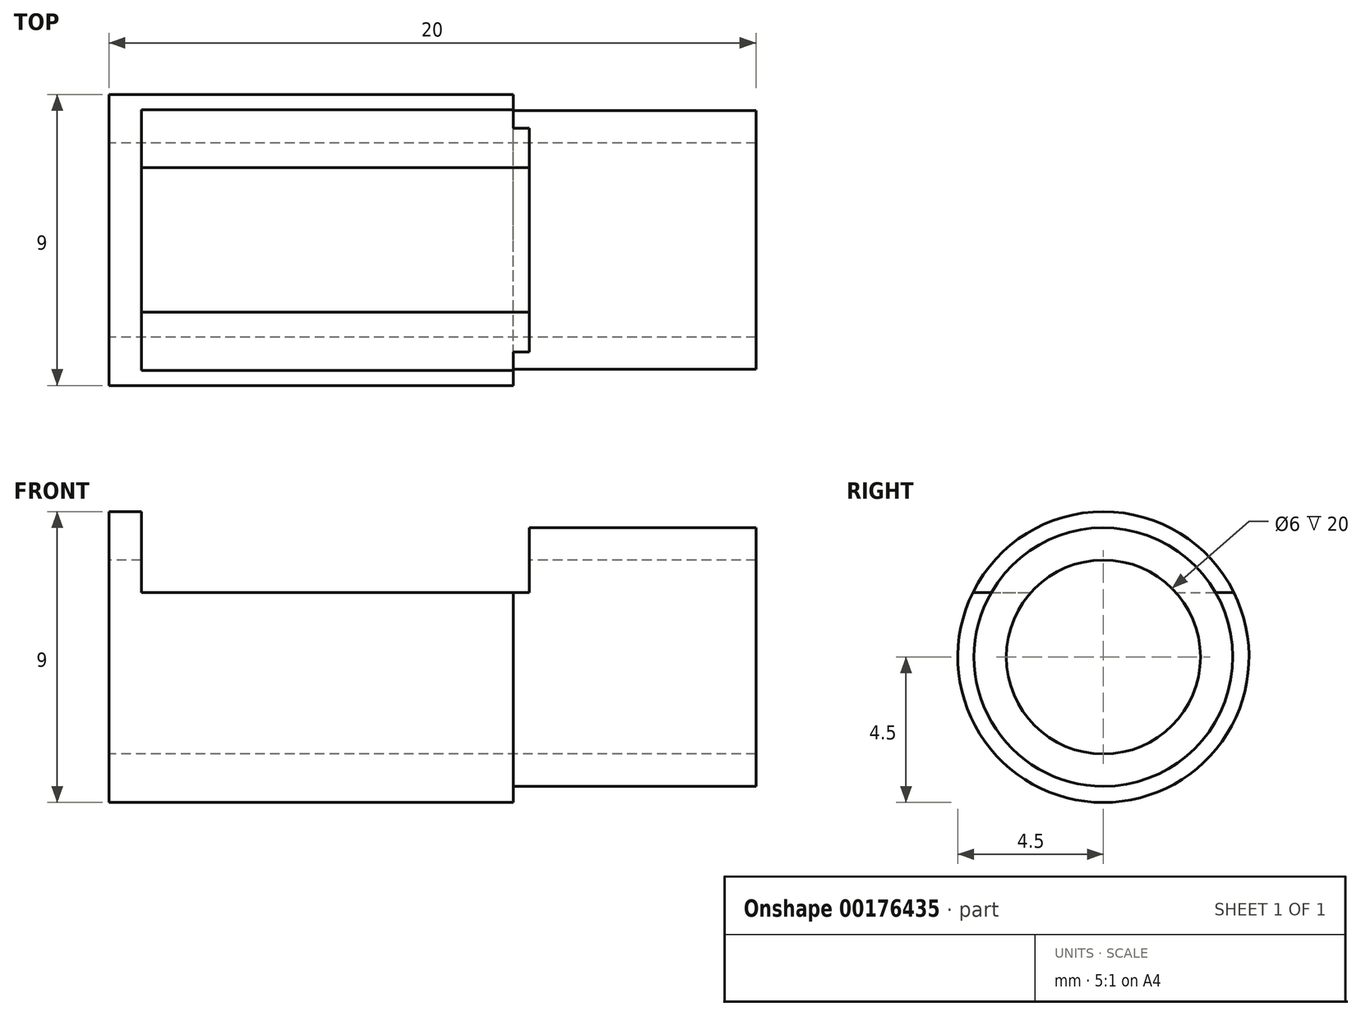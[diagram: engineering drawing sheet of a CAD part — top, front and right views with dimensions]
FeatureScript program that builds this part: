
annotation { "Feature Type Name" : "Feature", "Feature Type Description" : "" }
export const myFeature = defineFeature(function(context is Context, id is Id, definition is map)
    precondition{}
    {
        {
            var Q0;
            Q0=qCreatedBy(makeId("Right.planeOp"),FACE);
            var sketch = newSketch(context, id + "F0", { "sketchPlane" : qUnion([Q0])});
            skCircle(sketch, "E0", {"center": v(0, 0) * mm, "radius": 3 * mm});
            skCircle(sketch, "E1", {"center": v(0, 0) * mm, "radius": 4 * mm});
            skCircle(sketch, "E2", {"center": v(0, 0) * mm, "radius": 4.5 * mm});
            skSolve(sketch);
        }
        {
            var Q0;
            Q0=makeQuery(id+"F0.imprint","IMPRINT",FACE,{"disambiguationData":[TD([[makeQuery(id+"F0.imprint","IMPRINT",EDGE,{"derivedFrom":sQuery(id+"F0.wireOp",EDGE,"E0")}),-1.0]])]});
            extrude(context, id + "F1", {"entities" : qUnion([Q0]), "depth" : 7.5 * mm, "hasSecondDirection" : true, "secondDirectionOppositeDirection" : true, "secondDirectionDepth" : 12.5 * mm});
        }
        {
            var Q0;
            Q0=makeQuery(id+"F0.imprint","IMPRINT",FACE,{"disambiguationData":[TD([[makeQuery(id+"F0.imprint","IMPRINT",EDGE,{"derivedFrom":sQuery(id+"F0.wireOp",EDGE,"E1")}),-1.0]])]});
            extrude(context, id + "F2", {"entities" : qUnion([Q0]), "operationType" : NewBodyOperationType.ADD, "oppositeDirection" : true, "depth" : 12.5 * mm});
        }
        {
            var Q0;
            Q0=qCreatedBy(makeId("Front.planeOp"),FACE);
            var sketch = newSketch(context, id + "F3", { "sketchPlane" : qUnion([Q0])});
            skLineSegment(sketch, "E3.bottom", {"start": v(-11.5, 11.09) * mm, "end": v(0.5, 11.09) * mm});
            skLineSegment(sketch, "E3.top", {"start": v(-11.5, 2) * mm, "end": v(0.5, 2) * mm});
            skLineSegment(sketch, "E3.left", {"start": v(-11.5, 11.09) * mm, "end": v(-11.5, 2) * mm});
            skLineSegment(sketch, "E3.right", {"start": v(0.5, 11.09) * mm, "end": v(0.5, 2) * mm});
            skSolve(sketch);
        }
        {
            var Q0;
            Q0=makeQuery(id+"F3.imprint","IMPRINT",FACE,{"disambiguationData":[TD([[makeQuery(id+"F3.imprint","IMPRINT",EDGE,{"derivedFrom":sQuery(id+"F3.wireOp",EDGE,"E3.bottom")}),-1.0]])]});
            extrude(context, id + "F4", {"entities" : qUnion([Q0]), "operationType" : NewBodyOperationType.REMOVE, "depth" : 25 * mm, "hasSecondDirection" : true, "secondDirectionOppositeDirection" : true, "secondDirectionDepth" : 25 * mm});
        }
    });
